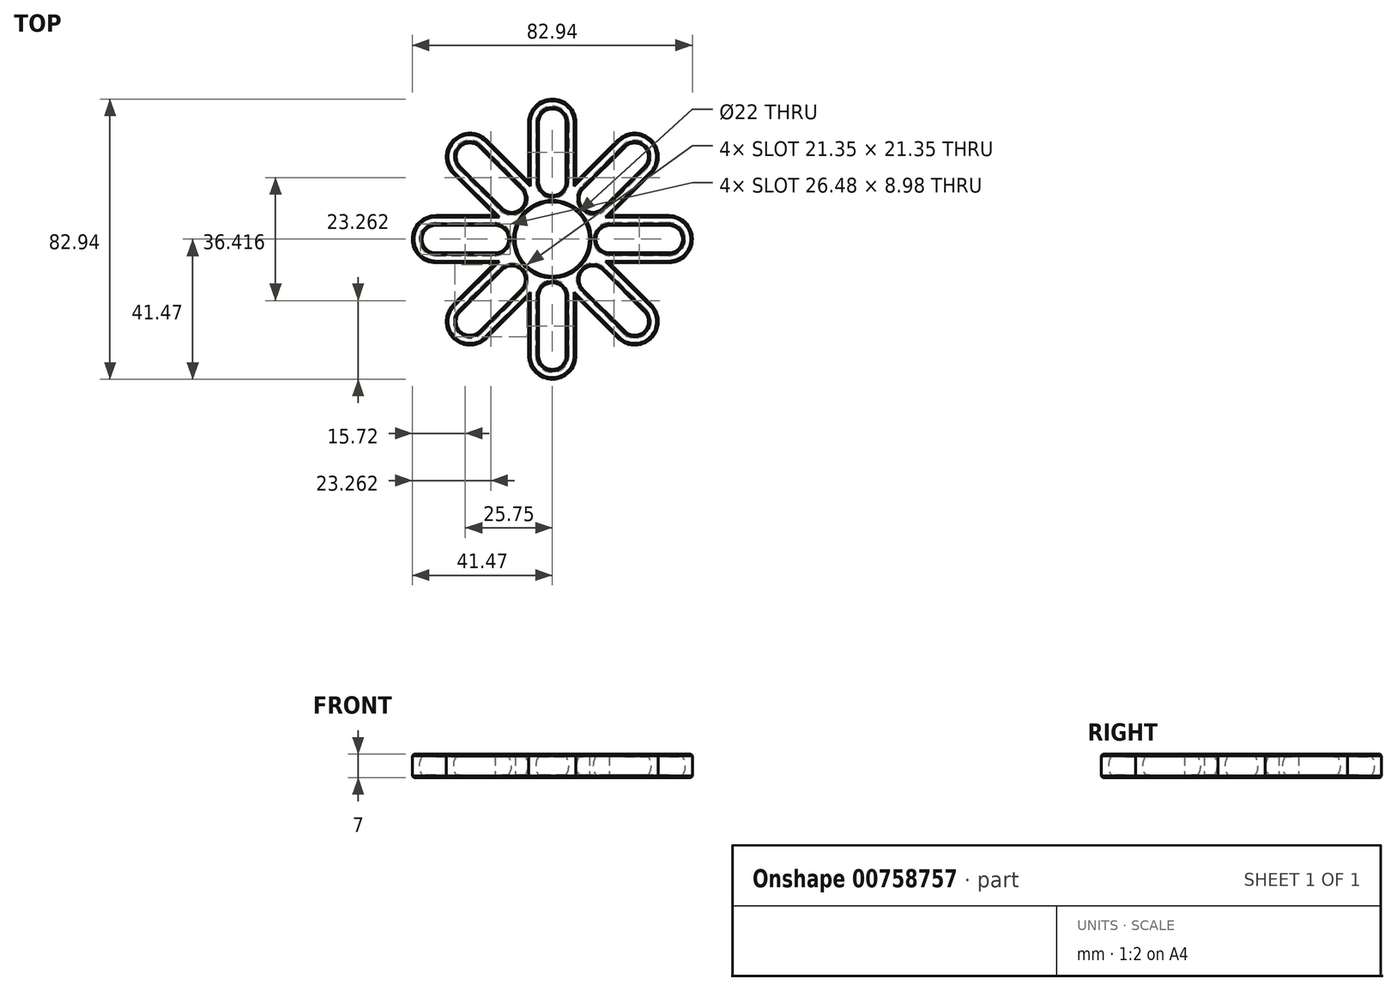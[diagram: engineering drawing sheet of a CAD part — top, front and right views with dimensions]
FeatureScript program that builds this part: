
annotation { "Feature Type Name" : "Feature", "Feature Type Description" : "" }
export const myFeature = defineFeature(function(context is Context, id is Id, definition is map)
    precondition{}
    {
        {
            var Q0;
            Q0=qCreatedBy(makeId("Top.planeOp"),FACE);
            var sketch = newSketch(context, id + "F0", { "sketchPlane" : qUnion([Q0])});
            skArc(sketch, "E0", {"start": v(7, 8.49) * mm, "mid": v(0, 11) * mm, "end": v(-7, 8.49) * mm});
            skArc(sketch, "E1", {"start": v(7, 12.12) * mm, "mid": v(0, 14) * mm, "end": v(-7, 12.12) * mm});
            skPoint(sketch, "E2", {"position": v(0, -24.5) * mm});
            skLineSegment(sketch, "E3", {"start": v(-7, 12.12) * mm, "end": v(-7, 34.47) * mm});
            skLineSegment(sketch, "E4", {"start": v(-7, 34.47) * mm, "end": v(7, 34.47) * mm});
            skLineSegment(sketch, "E5", {"start": v(7, 34.47) * mm, "end": v(7, 12.12) * mm});
            skArc(sketch, "E6", {"start": v(7, 34.47) * mm, "mid": v(0, 41.47) * mm, "end": v(-7, 34.47) * mm});
            skLineSegment(sketch, "E7", {"start": v(7, 12.12) * mm, "end": v(7, 8.49) * mm});
            skLineSegment(sketch, "E8", {"start": v(-7, 12.12) * mm, "end": v(-7, 8.49) * mm});
            skLineSegment(sketch, "E9", {"start": v(0, 0) * mm, "end": v(0, 68.94) * mm, "construction": true});
            skSolve(sketch);
        }
        {
            var Q0;
            Q0=makeQuery(id+"F0.imprint","IMPRINT",FACE,{"disambiguationData":[TD([[makeQuery(id+"F0.imprint","IMPRINT",EDGE,{"derivedFrom":sQuery(id+"F0.wireOp",EDGE,"E0")}),-1.0]])]});
            var Q1;
            {var subQ0=sQuery(id+"F0.wireOp",EDGE,"E3");Q1=makeQuery(id+"F0.imprint","IMPRINT",FACE,{"disambiguationData":[TD([[makeQuery(id+"F0.imprint","IMPRINT",EDGE,{"derivedFrom":subQ0}),-1.0]])]});}
            var Q2;
            Q2=makeQuery(id+"F0.imprint","IMPRINT",FACE,{"disambiguationData":[TD([[makeQuery(id+"F0.imprint","IMPRINT",EDGE,{"derivedFrom":sQuery(id+"F0.wireOp",EDGE,"E4")}),1.0]])]});
            extrude(context, id + "F1", {"entities" : qUnion([Q0, Q1, Q2]), "endBound" : BoundingType.SYMMETRIC, "depth" : 7 * mm, "offsetDistance" : 25 * mm});
        }
        {
            var Q0;
            Q0=qCreatedBy(makeId("Front.planeOp"),FACE);
            var sketch = newSketch(context, id + "F2", { "sketchPlane" : qUnion([Q0])});
            skLineSegment(sketch, "E10", {"start": v(0, 4.9) * mm, "end": v(0, -4.9) * mm});
            skArc(sketch, "E11", {"start": v(0, -4.9) * mm, "mid": v(4.9, 0) * mm, "end": v(0, 4.9) * mm});
            skArc(sketch, "E12.MirrorCS", {"start": v(0, -4.9) * mm, "mid": v(-4.9, 0) * mm, "end": v(0, 4.9) * mm});
            skSolve(sketch);
        }
        {
            var Q0;
            Q0 = qSketchRegion(id + "F2", true);
            extrude(context, id + "F3", {"entities" : qUnion([Q0]), "operationType" : NewBodyOperationType.REMOVE, "oppositeDirection" : true, "depth" : 34.5 * mm, "offsetDistance" : 25 * mm, "hasSecondDirection" : true, "secondDirectionOppositeDirection" : true, "secondDirectionDepth" : 17 * mm});
        }
        {
            var Q0;
            Q0=makeQuery(id+"F3.boolean.opBoolean","COPY",FACE,{"derivedFrom":makeQuery(id+"F3.opExtrude","CAP_FACE",FACE,{"disambiguationData":[OSD([sQuery(id+"F2.wireOp",EDGE,"E11"),sQuery(id+"F2.wireOp",EDGE,"E12.MirrorCS")])],"isStart":false})});
            var sketch = newSketch(context, id + "F4", { "sketchPlane" : qUnion([Q0])});
            skArc(sketch, "E13", {"start": v(0, -4.9) * mm, "mid": v(4.9, 0) * mm, "end": v(0, 4.9) * mm});
            skLineSegment(sketch, "E14", {"start": v(0, -4.9) * mm, "end": v(0, 4.9) * mm});
            skSolve(sketch);
        }
        {
            var Q0;
            Q0 = qSketchRegion(id + "F4", true);
            var Q1;
            Q1=sQuery(id+"F4.wireOp",EDGE,"E14");
            revolve(context, id + "F5", {"operationType" : NewBodyOperationType.REMOVE, "surfaceOperationType" : NewSurfaceOperationType.NEW, "entities" : qUnion([Q0]), "axis" : qUnion([Q1]), "revolveType" : RevolveType.FULL});
        }
        {
            var Q0;
            Q0=makeQuery(id+"F3.boolean.opBoolean","COPY",FACE,{"derivedFrom":makeQuery(id+"F3.opExtrude","CAP_FACE",FACE,{"disambiguationData":[OSD([sQuery(id+"F2.wireOp",EDGE,"E11"),sQuery(id+"F2.wireOp",EDGE,"E12.MirrorCS")])],"isStart":true})});
            var sketch = newSketch(context, id + "F6", { "sketchPlane" : qUnion([Q0])});
            skArc(sketch, "E15", {"start": v(0, -4.9) * mm, "mid": v(4.9, 0) * mm, "end": v(0, 4.9) * mm});
            skLineSegment(sketch, "E16", {"start": v(0, 4.9) * mm, "end": v(0, -4.9) * mm});
            skSolve(sketch);
        }
        {
            var Q0;
            Q0 = qSketchRegion(id + "F6", true);
            var Q1;
            Q1=sQuery(id+"F6.wireOp",EDGE,"E16");
            revolve(context, id + "F7", {"operationType" : NewBodyOperationType.REMOVE, "surfaceOperationType" : NewSurfaceOperationType.NEW, "entities" : qUnion([Q0]), "axis" : qUnion([Q1]), "revolveType" : RevolveType.FULL, "oppositeDirection" : true});
        }
        {
            var Q0;
            Q0=makeQuery(id+"F1.opExtrude","SWEPT_BODY",BODY,{"disambiguationData":[OSD([sQuery(id+"F0.wireOp",EDGE,"E0"),sQuery(id+"F0.wireOp",EDGE,"E1"),sQuery(id+"F0.wireOp",EDGE,"E3"),sQuery(id+"F0.wireOp",EDGE,"E5"),sQuery(id+"F0.wireOp",EDGE,"E6")])]});
            var Q1;
            Q1=sQuery(id+"F2.wireOp",EDGE,"E10");
            circularPattern(context, id + "F8", {"operationType" : NewBodyOperationType.ADD, "entities" : qUnion([Q0]), "axis" : qUnion([Q1]), "angle" : 360 * degree, "instanceCount" : 8, "equalSpace" : true});
        }
        {
            var Q0;
            {var subQ0=makeQuery(id+"F1.opExtrude","CAP_FACE",FACE,{"disambiguationData":[OSD([sQuery(id+"F0.wireOp",EDGE,"E0"),sQuery(id+"F0.wireOp",EDGE,"E3"),sQuery(id+"F0.wireOp",EDGE,"E5"),sQuery(id+"F0.wireOp",EDGE,"E6"),sQuery(id+"F0.wireOp",EDGE,"E7"),sQuery(id+"F0.wireOp",EDGE,"E8")])],"isStart":false});Q0=makeQuery(id+"F8.boolean.opBoolean","MERGE",FACE,{"derivedFrom":[subQ0,makeQuery(id+"F8.opPattern","COPY",FACE,{"derivedFrom":subQ0,"instanceName":"1"}),makeQuery(id+"F8.opPattern","COPY",FACE,{"derivedFrom":subQ0,"instanceName":"2"}),makeQuery(id+"F8.opPattern","COPY",FACE,{"derivedFrom":subQ0,"instanceName":"3"}),makeQuery(id+"F8.opPattern","COPY",FACE,{"derivedFrom":subQ0,"instanceName":"4"}),makeQuery(id+"F8.opPattern","COPY",FACE,{"derivedFrom":subQ0,"instanceName":"5"}),makeQuery(id+"F8.opPattern","COPY",FACE,{"derivedFrom":subQ0,"instanceName":"6"}),makeQuery(id+"F8.opPattern","COPY",FACE,{"derivedFrom":subQ0,"instanceName":"7"})]});}
            var Q1;
            {var subQ0=makeQuery(id+"F1.opExtrude","CAP_FACE",FACE,{"disambiguationData":[OSD([sQuery(id+"F0.wireOp",EDGE,"E0"),sQuery(id+"F0.wireOp",EDGE,"E3"),sQuery(id+"F0.wireOp",EDGE,"E5"),sQuery(id+"F0.wireOp",EDGE,"E6"),sQuery(id+"F0.wireOp",EDGE,"E7"),sQuery(id+"F0.wireOp",EDGE,"E8")])],"isStart":true});Q1=makeQuery(id+"F8.boolean.opBoolean","MERGE",FACE,{"derivedFrom":[subQ0,makeQuery(id+"F8.opPattern","COPY",FACE,{"derivedFrom":subQ0,"instanceName":"1"}),makeQuery(id+"F8.opPattern","COPY",FACE,{"derivedFrom":subQ0,"instanceName":"2"}),makeQuery(id+"F8.opPattern","COPY",FACE,{"derivedFrom":subQ0,"instanceName":"3"}),makeQuery(id+"F8.opPattern","COPY",FACE,{"derivedFrom":subQ0,"instanceName":"4"}),makeQuery(id+"F8.opPattern","COPY",FACE,{"derivedFrom":subQ0,"instanceName":"5"}),makeQuery(id+"F8.opPattern","COPY",FACE,{"derivedFrom":subQ0,"instanceName":"6"}),makeQuery(id+"F8.opPattern","COPY",FACE,{"derivedFrom":subQ0,"instanceName":"7"})]});}
            chamfer(context, id + "F9", {"entities" : qUnion([Q0, Q1]), "width" : .5 * mm, "tangentPropagation" : true});
        }
    });
